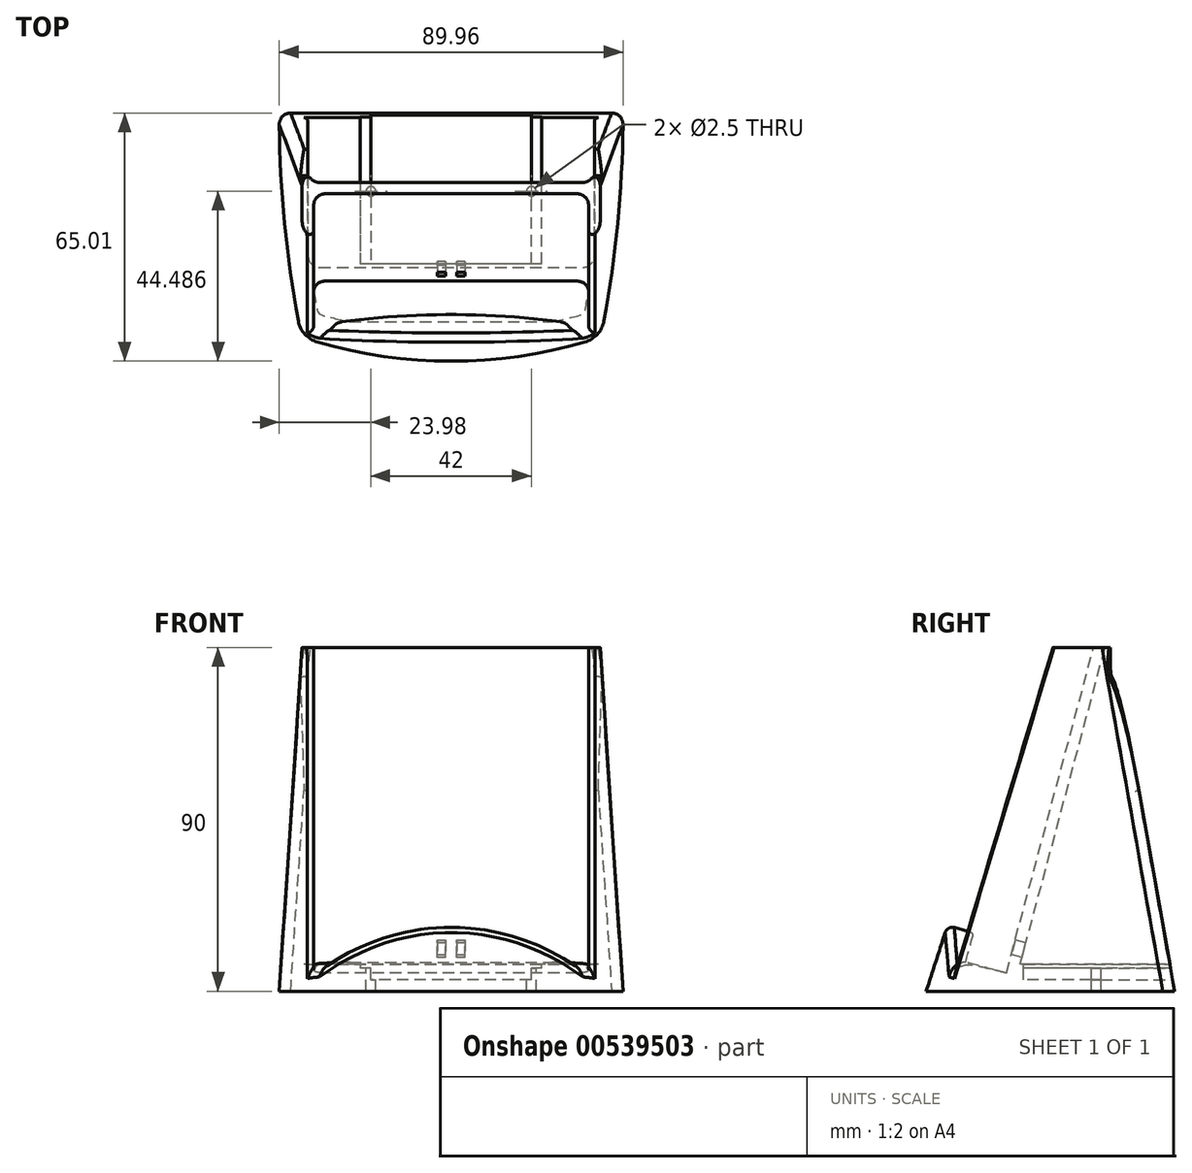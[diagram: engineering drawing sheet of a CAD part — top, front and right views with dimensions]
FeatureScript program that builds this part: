
annotation { "Feature Type Name" : "Feature", "Feature Type Description" : "" }
export const myFeature = defineFeature(function(context is Context, id is Id, definition is map)
    precondition{}
    {
        {
            var Q0;
            Q0=qCreatedBy(makeId("Right.planeOp"),FACE);
            var sketch = newSketch(context, id + "F0", { "sketchPlane" : qUnion([Q0])});
            skLineSegment(sketch, "E0", {"start": v(-3.77, 75.23) * mm, "end": v(-40, -60) * mm});
            skLineSegment(sketch, "E1", {"start": v(-40, -60) * mm, "end": v(-49.66, -57.41) * mm});
            skLineSegment(sketch, "E2", {"start": v(-49.66, -57.41) * mm, "end": v(-13.42, 77.82) * mm});
            skLineSegment(sketch, "E3", {"start": v(-13.42, 77.82) * mm, "end": v(-3.77, 75.23) * mm});
            skLineSegment(sketch, "E4", {"start": v(-40, -60) * mm, "end": v(-3.77, -60) * mm, "construction": true});
            skPoint(sketch, "E5", {"position": v(0, -65) * mm});
            skPoint(sketch, "E6", {"position": v(0, 25) * mm});
            skSolve(sketch);
        }
        {
            var Q0;
            Q0 = qSketchRegion(id + "F0", true);
            extrude(context, id + "F1", {"entities" : qUnion([Q0]), "endBound" : BoundingType.SYMMETRIC, "depth" : 70 * mm, "offsetDistance" : 25 * mm});
        }
        {
            var Q0;
            Q0=makeQuery(id+"F1.opExtrude","CAP_FACE",FACE,{"disambiguationData":[OSD([sQuery(id+"F0.wireOp",EDGE,"E0"),sQuery(id+"F0.wireOp",EDGE,"E1"),sQuery(id+"F0.wireOp",EDGE,"E2"),sQuery(id+"F0.wireOp",EDGE,"E3")])],"isStart":true});
            var sketch = newSketch(context, id + "F2", { "sketchPlane" : qUnion([Q0])});
            skLineSegment(sketch, "E7", {"start": v(10.58, 59.46) * mm, "end": v(18.34, 30.48) * mm});
            skLineSegment(sketch, "E8", {"start": v(18.34, 30.48) * mm, "end": v(23.17, 31.77) * mm});
            skLineSegment(sketch, "E9", {"start": v(23.17, 31.77) * mm, "end": v(15.4, 60.75) * mm});
            skLineSegment(sketch, "E10", {"start": v(15.4, 60.75) * mm, "end": v(10.58, 59.46) * mm});
            skLineSegment(sketch, "E11", {"start": v(8.6, 76.52) * mm, "end": v(13, 60.1) * mm, "construction": true});
            skSolve(sketch);
        }
        {
            var Q0;
            Q0 = qSketchRegion(id + "F2", true);
            extrude(context, id + "F3", {"entities" : qUnion([Q0]), "operationType" : NewBodyOperationType.ADD, "depth" : 1 * mm, "offsetDistance" : 25 * mm});
        }
        {
            var Q0;
            Q0=qCreatedBy(makeId("Top.planeOp"),FACE);
            var Q1;
            Q1=sQuery(id+"F0.wireOp",VERTEX,"E6");
            cPlane(context, id + "F4", {"entities" : qUnion([Q0, Q1]), "cplaneType" : CPlaneType.PLANE_POINT, "offset" : 25 * mm, "width" : 150 * mm, "height" : 150 * mm});
        }
        {
            var Q0;
            Q0=qCreatedBy(makeId("Top.planeOp"),FACE);
            var Q1;
            Q1=sQuery(id+"F0.wireOp",VERTEX,"E5");
            cPlane(context, id + "F5", {"entities" : qUnion([Q0, Q1]), "cplaneType" : CPlaneType.PLANE_POINT, "offset" : 25 * mm, "width" : 150 * mm, "height" : 150 * mm});
        }
        {
            var Q0;
            Q0=qCreatedBy(id+"F5.planeOp",FACE);
            var sketch = newSketch(context, id + "F6", { "sketchPlane" : qUnion([Q0])});
            skArc(sketch, "E12", {"start": v(-35, -55) * mm, "mid": v(0, -60) * mm, "end": v(35, -55) * mm});
            skLineSegment(sketch, "E13", {"start": v(-35, -55) * mm, "end": v(35, -55) * mm, "construction": true});
            skPoint(sketch, "E14", {"position": v(0, -60) * mm});
            skLineSegment(sketch, "E15", {"start": v(-45, 5) * mm, "end": v(45, 5) * mm});
            skPoint(sketch, "E16", {"position": v(0, 5) * mm});
            skArc(sketch, "E17", {"start": v(-45, 5) * mm, "mid": v(-43.75, -22.35) * mm, "end": v(-40, -49.47) * mm});
            skArc(sketch, "E18", {"start": v(-40, -49.47) * mm, "mid": v(-38.28, -52.94) * mm, "end": v(-35, -55) * mm});
            skArc(sketch, "E19", {"start": v(35, -55) * mm, "mid": v(38.28, -52.94) * mm, "end": v(40, -49.47) * mm});
            skArc(sketch, "E20", {"start": v(40, -49.47) * mm, "mid": v(43.75, -22.35) * mm, "end": v(45, 5) * mm});
            skSolve(sketch);
        }
        {
            var Q0;
            Q0=qCreatedBy(id+"F4.planeOp",FACE);
            var sketch = newSketch(context, id + "F7", { "sketchPlane" : qUnion([Q0])});
            skArc(sketch, "E21", {"start": v(-35, -28) * mm, "mid": v(0, -31) * mm, "end": v(35, -28) * mm});
            skLineSegment(sketch, "E22", {"start": v(-35, -28) * mm, "end": v(35, -28) * mm, "construction": true});
            skPoint(sketch, "E23", {"position": v(0, -28) * mm});
            skPoint(sketch, "E24", {"position": v(0, -31) * mm});
            skLineSegment(sketch, "E25", {"start": v(39, -11) * mm, "end": v(-39, -11) * mm});
            skPoint(sketch, "E26", {"position": v(0, -11) * mm});
            skLineSegment(sketch, "E27", {"start": v(-39, -11) * mm, "end": v(-39, -23.25) * mm});
            skLineSegment(sketch, "E28", {"start": v(39, -11) * mm, "end": v(39, -23.25) * mm});
            skArc(sketch, "E29", {"start": v(-39, -23.25) * mm, "mid": v(-37.87, -26.35) * mm, "end": v(-35, -28) * mm});
            skArc(sketch, "E30", {"start": v(35, -28) * mm, "mid": v(37.87, -26.35) * mm, "end": v(39, -23.25) * mm});
            skSolve(sketch);
        }
        {
            var Q1;
            Q1=makeQuery(id+"F6.imprint","IMPRINT",FACE,{"disambiguationData":[TD([[makeQuery(id+"F6.imprint","IMPRINT",EDGE,{"derivedFrom":sQuery(id+"F6.wireOp",EDGE,"E12")}),1.0]])]});
            var Q2;
            Q2=makeQuery(id+"F7.imprint","IMPRINT",FACE,{"disambiguationData":[TD([[makeQuery(id+"F7.imprint","IMPRINT",EDGE,{"derivedFrom":sQuery(id+"F7.wireOp",EDGE,"E21")}),1.0]])]});
            loft(context, id + "F8", {"sheetProfilesArray" : [{ "sheetProfileEntities" : qUnion([Q1]) }, { "sheetProfileEntities" : qUnion([Q2]) }]});
        }
        {
            var Q0;
            Q0=makeQuery(id+"F1.opExtrude","SWEPT_FACE",FACE,{"disambiguationData":[OSD([sQuery(id+"F0.wireOp",EDGE,"E3")])]});
            var sketch = newSketch(context, id + "F9", { "sketchPlane" : qUnion([Q0])});
            skLineSegment(sketch, "E31.0", {"start": v(36, -33.1) * mm, "end": v(36, -22.1) * mm});
            skLineSegment(sketch, "E31.1", {"start": v(36, -22.1) * mm, "end": v(-36, -22.1) * mm});
            skLineSegment(sketch, "E31.2", {"start": v(-36, -33.1) * mm, "end": v(-36, -22.1) * mm});
            skLineSegment(sketch, "E32", {"start": v(-36, -33.1) * mm, "end": v(36, -33.1) * mm});
            skSolve(sketch);
        }
        {
            var Q0;
            Q0 = qSketchRegion(id + "F9", true);
            extrude(context, id + "F10", {"entities" : qUnion([Q0]), "operationType" : NewBodyOperationType.REMOVE, "oppositeDirection" : true, "depth" : 140 * mm, "offsetDistance" : 25 * mm});
        }
        {
            var Q0;
            Q0=makeQuery(id+"F10.boolean.opBoolean","COPY",FACE,{"derivedFrom":makeQuery(id+"F10.opExtrude","SWEPT_FACE",FACE,{"disambiguationData":[OSD([sQuery(id+"F9.wireOp",EDGE,"E31.1")])]})});
            var sketch = newSketch(context, id + "F11", { "sketchPlane" : qUnion([Q0])});
            skLineSegment(sketch, "E33", {"start": v(-36, -68.3) * mm, "end": v(-36, 19.96) * mm});
            skLineSegment(sketch, "E34", {"start": v(-36, 19.96) * mm, "end": v(36, 19.96) * mm});
            skLineSegment(sketch, "E35", {"start": v(36, 19.96) * mm, "end": v(36, -68.3) * mm});
            skLineSegment(sketch, "E36", {"start": v(36, -68.3) * mm, "end": v(30, -68.3) * mm});
            skLineSegment(sketch, "E37", {"start": v(-36, -68.3) * mm, "end": v(-30, -68.3) * mm});
            skArc(sketch, "E38", {"start": v(30, -68.3) * mm, "mid": v(0, -60.3) * mm, "end": v(-30, -68.3) * mm});
            skPoint(sketch, "E39", {"position": v(0, -60.3) * mm});
            skLineSegment(sketch, "E40", {"start": v(-30, -68.3) * mm, "end": v(30, -68.3) * mm, "construction": true});
            skSolve(sketch);
        }
        {
            var Q0;
            Q0 = qSketchRegion(id + "F11", true);
            extrude(context, id + "F12", {"entities" : qUnion([Q0]), "operationType" : NewBodyOperationType.REMOVE, "endBound" : BoundingType.THROUGH_ALL, "depth" : 55.9 * mm, "offsetDistance" : 25 * mm});
        }
        {
            var Q0;
            Q0=makeQuery(id+"F12.boolean.opBoolean","INTERSECT",EDGE,{"derivedFrom":[makeQuery(id+"F8.opLoft","SWEPT_FACE",FACE,{"disambiguationData":[OSD([sQuery(id+"F6.wireOp",EDGE,"E15"),sQuery(id+"F6.wireOp",EDGE,"E17"),sQuery(id+"F6.wireOp",EDGE,"E18"),sQuery(id+"F7.wireOp",EDGE,"E25"),sQuery(id+"F7.wireOp",EDGE,"E27"),sQuery(id+"F7.wireOp",EDGE,"E29")])]}),makeQuery(id+"F12.opExtrude","SWEPT_FACE",FACE,{"disambiguationData":[OSD([sQuery(id+"F11.wireOp",EDGE,"E33")])]})]});
            var Q1;
            Q1=makeQuery(id+"F12.boolean.opBoolean","INTERSECT",EDGE,{"derivedFrom":[makeQuery(id+"F8.opLoft","SWEPT_FACE",FACE,{"disambiguationData":[OSD([sQuery(id+"F6.wireOp",EDGE,"E15"),sQuery(id+"F6.wireOp",EDGE,"E17"),sQuery(id+"F6.wireOp",EDGE,"E18"),sQuery(id+"F7.wireOp",EDGE,"E25"),sQuery(id+"F7.wireOp",EDGE,"E27"),sQuery(id+"F7.wireOp",EDGE,"E29")])]}),makeQuery(id+"F12.opExtrude","SWEPT_FACE",FACE,{"disambiguationData":[OSD([sQuery(id+"F11.wireOp",EDGE,"E35")])]})]});
            fillet(context, id + "F13", {"entities" : qUnion([Q0, Q1]), "radius" : 1 * mm, "tangentPropagation" : true, "allowEdgeOverflow" : false});
        }
        {
            var Q0;
            Q0=makeQuery(id+"F12.boolean.opBoolean","INTERSECT",EDGE,{"derivedFrom":[makeQuery(id+"F8.opLoft","SWEPT_FACE",FACE,{"disambiguationData":[OSD([sQuery(id+"F6.wireOp",EDGE,"E15"),sQuery(id+"F6.wireOp",EDGE,"E17"),sQuery(id+"F6.wireOp",EDGE,"E18"),sQuery(id+"F7.wireOp",EDGE,"E25"),sQuery(id+"F7.wireOp",EDGE,"E27"),sQuery(id+"F7.wireOp",EDGE,"E29")])]}),makeQuery(id+"F12.opExtrude","SWEPT_FACE",FACE,{"disambiguationData":[OSD([sQuery(id+"F11.wireOp",EDGE,"E37")])]})]});
            var Q1;
            Q1=makeQuery(id+"F12.boolean.opBoolean","INTERSECT",EDGE,{"derivedFrom":[makeQuery(id+"F8.opLoft","SWEPT_FACE",FACE,{"disambiguationData":[OSD([sQuery(id+"F6.wireOp",EDGE,"E15"),sQuery(id+"F6.wireOp",EDGE,"E17"),sQuery(id+"F6.wireOp",EDGE,"E18"),sQuery(id+"F7.wireOp",EDGE,"E25"),sQuery(id+"F7.wireOp",EDGE,"E27"),sQuery(id+"F7.wireOp",EDGE,"E29")])]}),makeQuery(id+"F12.opExtrude","SWEPT_FACE",FACE,{"disambiguationData":[OSD([sQuery(id+"F11.wireOp",EDGE,"E36")])]})]});
            fillet(context, id + "F14", {"entities" : qUnion([Q0, Q1]), "radius" : 5 * mm, "tangentPropagation" : true, "allowEdgeOverflow" : false});
        }
        {
            var Q0;
            Q0=makeQuery(id+"F12.boolean.opBoolean","INTERSECT",EDGE,{"derivedFrom":[makeQuery(id+"F8.opLoft","SWEPT_FACE",FACE,{"disambiguationData":[OSD([sQuery(id+"F6.wireOp",EDGE,"E15"),sQuery(id+"F6.wireOp",EDGE,"E17"),sQuery(id+"F6.wireOp",EDGE,"E18"),sQuery(id+"F7.wireOp",EDGE,"E25"),sQuery(id+"F7.wireOp",EDGE,"E27"),sQuery(id+"F7.wireOp",EDGE,"E29")])]}),makeQuery(id+"F12.opExtrude","SWEPT_FACE",FACE,{"disambiguationData":[OSD([sQuery(id+"F11.wireOp",EDGE,"E38")])]})]});
            fillet(context, id + "F15", {"entities" : qUnion([Q0]), "radius" : 2 * mm, "tangentPropagation" : true, "allowEdgeOverflow" : false});
        }
        {
            var Q0;
            Q0=makeQuery(id+"F12.boolean.opBoolean","INTERSECT",EDGE,{"derivedFrom":[makeQuery(id+"F10.boolean.opBoolean","COPY",FACE,{"derivedFrom":makeQuery(id+"F10.opExtrude","SWEPT_FACE",FACE,{"disambiguationData":[OSD([sQuery(id+"F9.wireOp",EDGE,"E32")])]})}),makeQuery(id+"F12.opExtrude","SWEPT_FACE",FACE,{"disambiguationData":[OSD([sQuery(id+"F11.wireOp",EDGE,"E38")])]})]});
            fillet(context, id + "F16", {"entities" : qUnion([Q0]), "radius" : 1 * mm, "tangentPropagation" : true, "allowEdgeOverflow" : false});
        }
        {
            var Q0;
            Q0=makeQuery(id+"F10.boolean.opBoolean","COPY",EDGE,{"derivedFrom":makeQuery(id+"F10.opExtrude","SWEPT_EDGE",EDGE,{"disambiguationData":[OSD([sQuery(id+"F9.wireOp",EDGE,"E31.0"),sQuery(id+"F9.wireOp",EDGE,"E31.1")])]})});
            var Q1;
            Q1=makeQuery(id+"F10.boolean.opBoolean","COPY",EDGE,{"derivedFrom":makeQuery(id+"F10.opExtrude","SWEPT_EDGE",EDGE,{"disambiguationData":[OSD([sQuery(id+"F9.wireOp",EDGE,"E31.1"),sQuery(id+"F9.wireOp",EDGE,"E31.2")])]})});
            fillet(context, id + "F17", {"entities" : qUnion([Q0, Q1]), "radius" : 3 * mm, "tangentPropagation" : true, "allowEdgeOverflow" : false});
        }
        {
            var Q0;
            Q0=qCreatedBy(makeId("Right.planeOp"),FACE);
            var sketch = newSketch(context, id + "F18", { "sketchPlane" : qUnion([Q0])});
            skLineSegment(sketch, "E41", {"start": v(7.44, 102) * mm, "end": v(7.44, -58) * mm});
            skLineSegment(sketch, "E42", {"start": v(7.44, -58) * mm, "end": v(-35.43, -58) * mm});
            skLineSegment(sketch, "E43", {"start": v(-35.43, -58) * mm, "end": v(7.44, 102) * mm});
            skPoint(sketch, "E44", {"position": v(-13.19, 25) * mm});
            skSolve(sketch);
        }
        {
            var Q0;
            Q0 = qSketchRegion(id + "F18", true);
            extrude(context, id + "F19", {"entities" : qUnion([Q0]), "operationType" : NewBodyOperationType.REMOVE, "endBound" : BoundingType.SYMMETRIC, "oppositeDirection" : true, "depth" : 75 * mm, "offsetDistance" : 25 * mm});
        }
        {
            var Q0;
            Q0=makeQuery(id+"F19.boolean.opBoolean","COPY",FACE,{"derivedFrom":makeQuery(id+"F19.opExtrude","CAP_FACE",FACE,{"disambiguationData":[OSD([sQuery(id+"F18.wireOp",EDGE,"E41"),sQuery(id+"F18.wireOp",EDGE,"E42"),sQuery(id+"F18.wireOp",EDGE,"E43")])],"isStart":true})});
            var sketch = newSketch(context, id + "F20", { "sketchPlane" : qUnion([Q0])});
            skLineSegment(sketch, "E45", {"start": v(-2.49, -50.86) * mm, "end": v(33.51, -50.86) * mm});
            skPoint(sketch, "E46", {"position": v(15.51, -50.86) * mm});
            skSolve(sketch);
        }
        {
            var Q0;
            Q0=makeQuery(id+"F19.boolean.opBoolean","COPY",FACE,{"derivedFrom":makeQuery(id+"F19.opExtrude","SWEPT_FACE",FACE,{"disambiguationData":[OSD([sQuery(id+"F18.wireOp",EDGE,"E42")])]})});
            var sketch = newSketch(context, id + "F21", { "sketchPlane" : qUnion([Q0])});
            skLineSegment(sketch, "E47.bottom", {"start": v(23.75, -34.51) * mm, "end": v(-23.75, -34.51) * mm});
            skLineSegment(sketch, "E47.top", {"start": v(23.75, 3.49) * mm, "end": v(-23.75, 3.49) * mm, "construction": true});
            skLineSegment(sketch, "E47.left", {"start": v(23.75, -34.51) * mm, "end": v(23.75, 3.49) * mm});
            skLineSegment(sketch, "E47.right", {"start": v(-23.75, -34.51) * mm, "end": v(-23.75, 3.49) * mm});
            skPoint(sketch, "E48", {"position": v(23.75, -15.51) * mm});
            skLineSegment(sketch, "E49", {"start": v(23.75, 3.49) * mm, "end": v(23.75, 15.49) * mm});
            skLineSegment(sketch, "E50", {"start": v(23.75, 15.49) * mm, "end": v(-23.75, 15.49) * mm});
            skLineSegment(sketch, "E51", {"start": v(-23.75, 15.49) * mm, "end": v(-23.75, 3.49) * mm});
            skPoint(sketch, "E52", {"position": v(0, 15.49) * mm});
            skSolve(sketch);
        }
        {
            var Q0;
            Q0 = qSketchRegion(id + "F21", true);
            extrude(context, id + "F22", {"entities" : qUnion([Q0]), "operationType" : NewBodyOperationType.REMOVE, "oppositeDirection" : true, "depth" : 1 * mm, "offsetDistance" : 25 * mm});
        }
        {
            var Q0;
            Q0=makeQuery(id+"F22.boolean.opBoolean","COPY",FACE,{"derivedFrom":makeQuery(id+"F22.opExtrude","CAP_FACE",FACE,{"disambiguationData":[OSD([sQuery(id+"F21.wireOp",EDGE,"E47.bottom"),sQuery(id+"F21.wireOp",EDGE,"E47.left"),sQuery(id+"F21.wireOp",EDGE,"E47.right"),sQuery(id+"F21.wireOp",EDGE,"E49"),sQuery(id+"F21.wireOp",EDGE,"E50"),sQuery(id+"F21.wireOp",EDGE,"E51")])],"isStart":false})});
            var sketch = newSketch(context, id + "F23", { "sketchPlane" : qUnion([Q0])});
            skLineSegment(sketch, "E53.bottom", {"start": v(21, -34.51) * mm, "end": v(-21, -34.51) * mm});
            skLineSegment(sketch, "E53.top", {"start": v(21, 3.93) * mm, "end": v(-21, 3.93) * mm, "construction": true});
            skLineSegment(sketch, "E53.left", {"start": v(21, -34.51) * mm, "end": v(21, 3.93) * mm});
            skLineSegment(sketch, "E53.right", {"start": v(-21, -34.51) * mm, "end": v(-21, 3.93) * mm});
            skPoint(sketch, "E54", {"position": v(0, 3.93) * mm});
            skLineSegment(sketch, "E55", {"start": v(21, 3.93) * mm, "end": v(21, 4.93) * mm});
            skLineSegment(sketch, "E56", {"start": v(21, 4.93) * mm, "end": v(-21, 4.93) * mm});
            skLineSegment(sketch, "E57", {"start": v(-21, 4.93) * mm, "end": v(-21, 3.93) * mm});
            skSolve(sketch);
        }
        {
            var Q0;
            Q0 = qSketchRegion(id + "F23", true);
            extrude(context, id + "F24", {"entities" : qUnion([Q0]), "operationType" : NewBodyOperationType.REMOVE, "oppositeDirection" : true, "depth" : 3 * mm, "offsetDistance" : 25 * mm});
        }
        {
            var Q0;
            Q0=makeQuery(id+"F19.boolean.opBoolean","COPY",FACE,{"derivedFrom":makeQuery(id+"F19.opExtrude","SWEPT_FACE",FACE,{"disambiguationData":[OSD([sQuery(id+"F18.wireOp",EDGE,"E42")])]})});
            var sketch = newSketch(context, id + "F25", { "sketchPlane" : qUnion([Q0])});
            skCircle(sketch, "E58", {"center": v(21, -15.51) * mm, "radius": 1.25 * mm});
            skCircle(sketch, "E59", {"center": v(-21, -15.51) * mm, "radius": 1.25 * mm});
            skSolve(sketch);
        }
        {
            var Q0;
            Q0 = qSketchRegion(id + "F25", true);
            extrude(context, id + "F26", {"entities" : qUnion([Q0]), "operationType" : NewBodyOperationType.REMOVE, "oppositeDirection" : true, "depth" : 25 * mm, "offsetDistance" : 25 * mm});
        }
        {
            var Q0;
            Q0=makeQuery(id+"F10.boolean.opBoolean","COPY",FACE,{"derivedFrom":makeQuery(id+"F10.opExtrude","SWEPT_FACE",FACE,{"disambiguationData":[OSD([sQuery(id+"F9.wireOp",EDGE,"E31.1")])]})});
            var sketch = newSketch(context, id + "F27", { "sketchPlane" : qUnion([Q0])});
            skLineSegment(sketch, "E60.bottom", {"start": v(-3.58, -59.3) * mm, "end": v(-1.5, -59.3) * mm});
            skLineSegment(sketch, "E60.top", {"start": v(-3.58, -63.3) * mm, "end": v(-1.5, -63.3) * mm});
            skLineSegment(sketch, "E60.left", {"start": v(-3.58, -59.3) * mm, "end": v(-3.58, -63.3) * mm});
            skLineSegment(sketch, "E60.right", {"start": v(-1.5, -59.3) * mm, "end": v(-1.5, -63.3) * mm});
            skLineSegment(sketch, "E61.bottom", {"start": v(1.5, -59.3) * mm, "end": v(3.58, -59.3) * mm});
            skLineSegment(sketch, "E61.top", {"start": v(1.5, -63.3) * mm, "end": v(3.58, -63.3) * mm});
            skLineSegment(sketch, "E61.left", {"start": v(1.5, -59.3) * mm, "end": v(1.5, -63.3) * mm});
            skLineSegment(sketch, "E61.right", {"start": v(3.58, -59.3) * mm, "end": v(3.58, -63.3) * mm});
            skLineSegment(sketch, "E62", {"start": v(-1.5, -59.3) * mm, "end": v(1.5, -59.3) * mm, "construction": true});
            skLineSegment(sketch, "E63", {"start": v(-1.5, -63.3) * mm, "end": v(1.5, -63.3) * mm, "construction": true});
            skPoint(sketch, "E64", {"position": v(-2.54, -59.3) * mm});
            skPoint(sketch, "E65", {"position": v(2.54, -59.3) * mm});
            skPoint(sketch, "E66", {"position": v(0, -59.3) * mm});
            skSolve(sketch);
        }
        {
            var Q0;
            Q0 = qSketchRegion(id + "F27", true);
            extrude(context, id + "F28", {"entities" : qUnion([Q0]), "operationType" : NewBodyOperationType.REMOVE, "oppositeDirection" : true, "depth" : 5 * mm, "offsetDistance" : 25 * mm});
        }
        {
            var Q0;
            Q0=makeQuery(id+"F19.boolean.opBoolean","COPY",EDGE,{"derivedFrom":makeQuery(id+"F19.opExtrude","CAP_EDGE",EDGE,{"disambiguationData":[OSD([sQuery(id+"F18.wireOp",EDGE,"E43")])],"isStart":true})});
            var Q1;
            Q1=makeQuery(id+"F19.boolean.opBoolean","COPY",EDGE,{"derivedFrom":makeQuery(id+"F19.opExtrude","CAP_EDGE",EDGE,{"disambiguationData":[OSD([sQuery(id+"F18.wireOp",EDGE,"E43")])],"isStart":false})});
            var Q2;
            Q2=makeQuery(id+"F8.opLoft","SWEPT_EDGE",EDGE,{"disambiguationData":[OSD([sQuery(id+"F6.wireOp",EDGE,"E15"),sQuery(id+"F6.wireOp",EDGE,"E17"),sQuery(id+"F7.wireOp",EDGE,"E25"),sQuery(id+"F7.wireOp",EDGE,"E27")])]});
            var Q3;
            Q3=makeQuery(id+"F8.opLoft","SWEPT_EDGE",EDGE,{"disambiguationData":[OSD([sQuery(id+"F6.wireOp",EDGE,"E15"),sQuery(id+"F6.wireOp",EDGE,"E20"),sQuery(id+"F7.wireOp",EDGE,"E25"),sQuery(id+"F7.wireOp",EDGE,"E28")])]});
            fillet(context, id + "F29", {"entities" : qUnion([Q0, Q1, Q2, Q3]), "radius" : 3 * mm, "tangentPropagation" : true, "allowEdgeOverflow" : false});
        }
        {
            var Q0;
            Q0=makeQuery(id+"F19.boolean.opBoolean","INTERSECT",EDGE,{"derivedFrom":[makeQuery(id+"F8.opLoft","SWEPT_FACE",FACE,{"disambiguationData":[OSD([sQuery(id+"F6.wireOp",EDGE,"E15"),sQuery(id+"F6.wireOp",EDGE,"E17"),sQuery(id+"F6.wireOp",EDGE,"E20"),sQuery(id+"F7.wireOp",EDGE,"E25"),sQuery(id+"F7.wireOp",EDGE,"E27"),sQuery(id+"F7.wireOp",EDGE,"E28")])]}),makeQuery(id+"F19.opExtrude","CAP_FACE",FACE,{"disambiguationData":[OSD([sQuery(id+"F18.wireOp",EDGE,"E41"),sQuery(id+"F18.wireOp",EDGE,"E42"),sQuery(id+"F18.wireOp",EDGE,"E43")])],"isStart":true})]});
            var Q1;
            Q1=makeQuery(id+"F19.boolean.opBoolean","INTERSECT",EDGE,{"derivedFrom":[makeQuery(id+"F8.opLoft","SWEPT_FACE",FACE,{"disambiguationData":[OSD([sQuery(id+"F6.wireOp",EDGE,"E15"),sQuery(id+"F6.wireOp",EDGE,"E17"),sQuery(id+"F6.wireOp",EDGE,"E20"),sQuery(id+"F7.wireOp",EDGE,"E25"),sQuery(id+"F7.wireOp",EDGE,"E27"),sQuery(id+"F7.wireOp",EDGE,"E28")])]}),makeQuery(id+"F19.opExtrude","CAP_FACE",FACE,{"disambiguationData":[OSD([sQuery(id+"F18.wireOp",EDGE,"E41"),sQuery(id+"F18.wireOp",EDGE,"E42"),sQuery(id+"F18.wireOp",EDGE,"E43")])],"isStart":false})]});
            fillet(context, id + "F30", {"entities" : qUnion([Q0, Q1]), "radius" : 1 * mm, "tangentPropagation" : true, "allowEdgeOverflow" : false});
        }
    });
